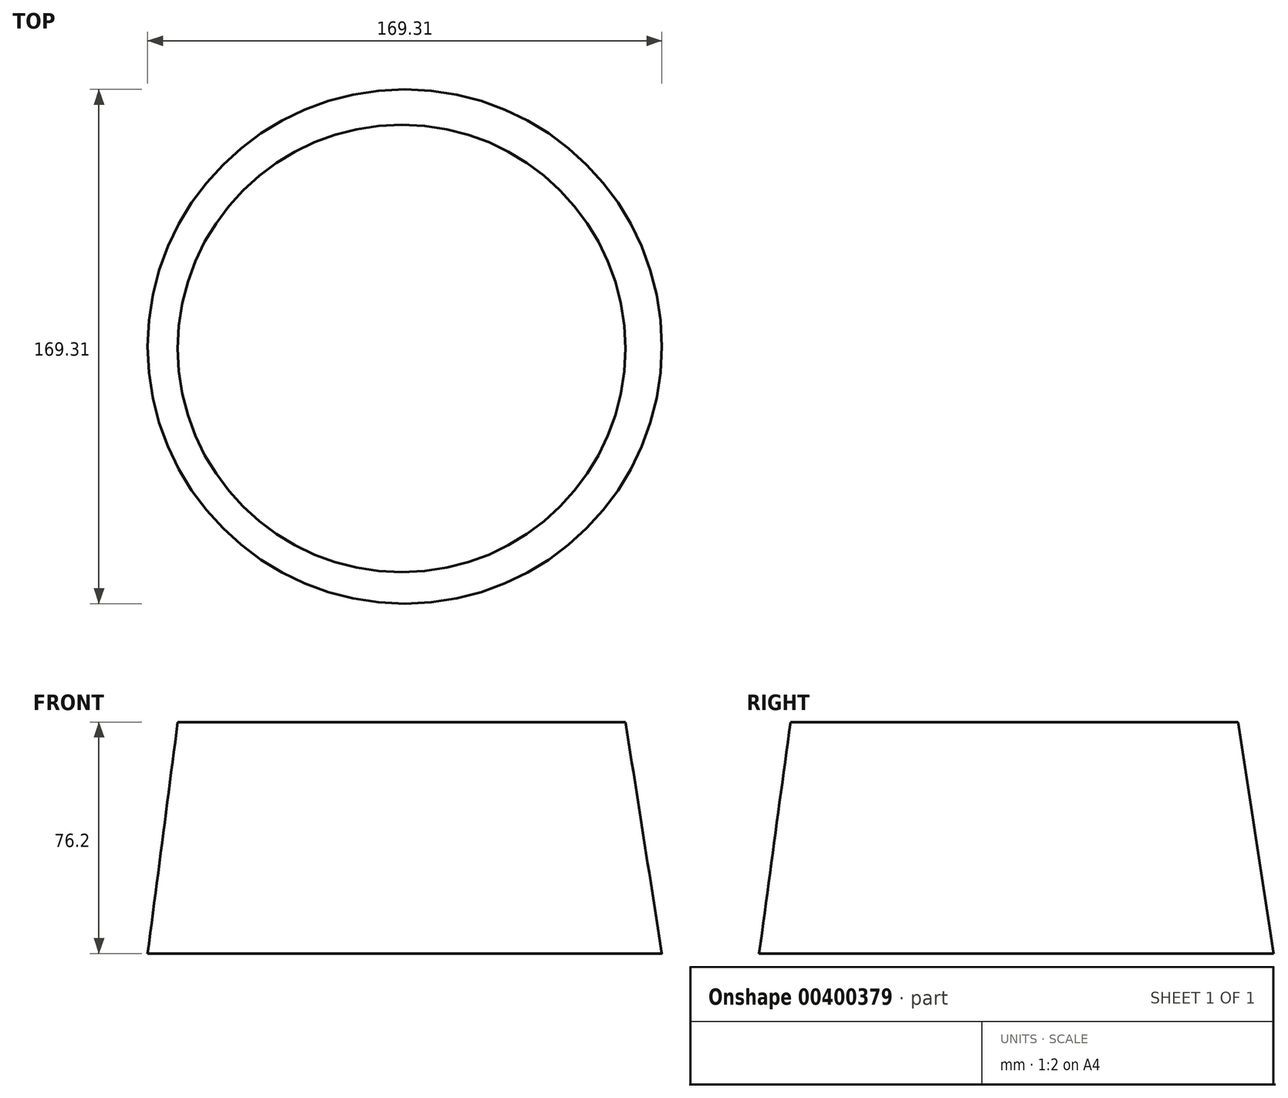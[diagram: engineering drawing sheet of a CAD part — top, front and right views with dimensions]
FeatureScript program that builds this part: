
annotation { "Feature Type Name" : "Feature", "Feature Type Description" : "" }
export const myFeature = defineFeature(function(context is Context, id is Id, definition is map)
    precondition{}
    {
        {
            var Q0;
            Q0=qCreatedBy(makeId("Top.planeOp"),FACE);
            var Q1;
            Q1 = qBodyType(qCreatedBy(id + "F1" ,EDGE), BodyType.WIRE);
            cPlane(context, id + "F0", {"entities" : qUnion([Q0, Q1]), "cplaneType" : CPlaneType.OFFSET, "offset" : 76.2 * mm, "width" : 152.4 * mm, "height" : 152.4 * mm});
        }
        {
            var Q0;
            Q0=qCreatedBy(id+"F0.planeOp",FACE);
            var sketch = newSketch(context, id + "F1", { "sketchPlane" : qUnion([Q0])});
            skCircle(sketch, "E0", {"center": v(-16.59, 21.4) * mm, "radius": 73.7 * mm});
            skSolve(sketch);
        }
        {
            var Q0;
            Q0=qCreatedBy(makeId("Top.planeOp"),FACE);
            var sketch = newSketch(context, id + "F2", { "sketchPlane" : qUnion([Q0])});
            skCircle(sketch, "E1", {"center": v(-15.55, 22.04) * mm, "radius": 84.65 * mm});
            skSolve(sketch);
        }
        {
            var Q0;
            Q0=makeQuery(id+"F1.imprint","IMPRINT",FACE,{"disambiguationData":[TD([[makeQuery(id+"F1.imprint","IMPRINT",EDGE,{"derivedFrom":sQuery(id+"F1.wireOp",EDGE,"E0")}),1.0]])]});
            var Q1;
            Q1 = qSketchRegion(id + "F2", true);
            loft(context, id + "F3", {"sheetProfilesArray" : [{ "sheetProfileEntities" : qUnion([Q0]) }, { "sheetProfileEntities" : qUnion([Q1]) }]});
        }
    });
